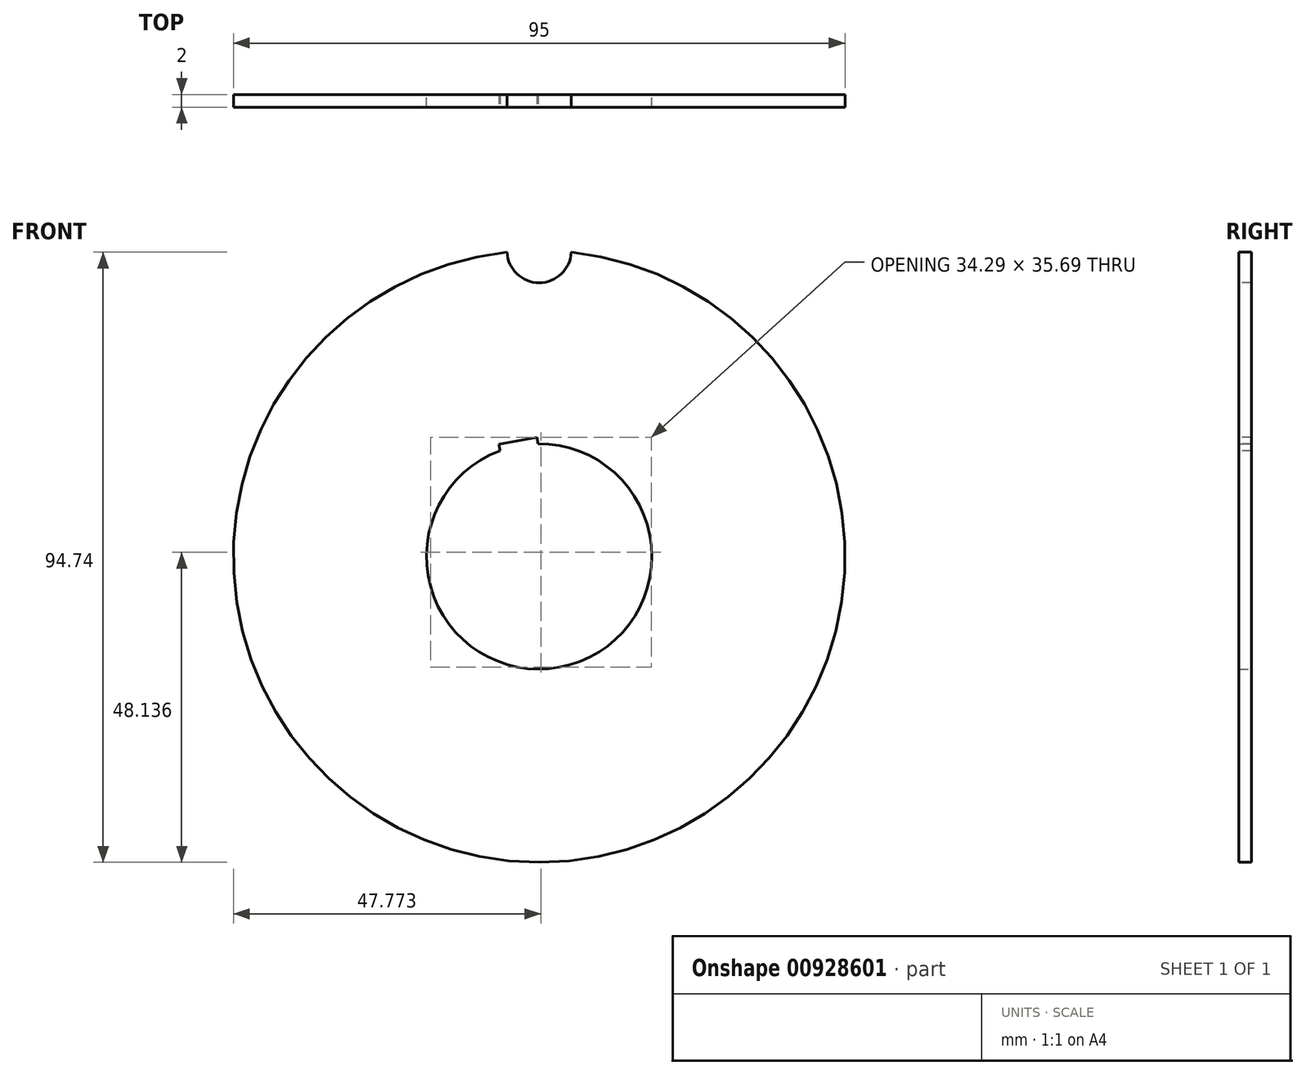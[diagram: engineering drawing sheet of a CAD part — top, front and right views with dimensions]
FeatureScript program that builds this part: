
annotation { "Feature Type Name" : "Feature", "Feature Type Description" : "" }
export const myFeature = defineFeature(function(context is Context, id is Id, definition is map)
    precondition{}
    {
        {
            var Q0;
            Q0=qCreatedBy(makeId("Front.planeOp"),FACE);
            var sketch = newSketch(context, id + "F0", { "sketchPlane" : qUnion([Q0])});
            skCircle(sketch, "E0", {"center": v(0, 0) * mm, "radius": 17.5 * mm});
            skCircle(sketch, "E1", {"center": v(0, 0) * mm, "radius": 47.5 * mm});
            skSolve(sketch);
        }
        {
            var Q0;
            Q0=makeQuery(id+"F0.imprint","IMPRINT",FACE,{"disambiguationData":[TD([[makeQuery(id+"F0.imprint","IMPRINT",EDGE,{"derivedFrom":sQuery(id+"F0.wireOp",EDGE,"E0")}),-1.0]])]});
            extrude(context, id + "F1", {"entities" : qUnion([Q0]), "depth" : 2 * mm, "offsetDistance" : 25 * mm});
        }
        {
            var Q0;
            Q0=makeQuery(id+"F1.opExtrude","CAP_FACE",FACE,{"disambiguationData":[OSD([sQuery(id+"F0.wireOp",EDGE,"E0"),sQuery(id+"F0.wireOp",EDGE,"E1")])],"isStart":false});
            var sketch = newSketch(context, id + "F2", { "sketchPlane" : qUnion([Q0])});
            skLineSegment(sketch, "E2", {"start": v(0, 0) * mm, "end": v(0, 47.5) * mm, "construction": true});
            skLineSegment(sketch, "E3", {"start": v(-5, 47.5) * mm, "end": v(5, 47.5) * mm, "construction": true});
            skArc(sketch, "E4", {"start": v(-5, 47.24) * mm, "mid": v(0, 42.5) * mm, "end": v(5, 47.24) * mm});
            skArc(sketch, "E5.0", {"start": v(5, 47.24) * mm, "mid": v(0, 47.5) * mm, "end": v(-5, 47.24) * mm});
            skSolve(sketch);
        }
        {
            var Q0;
            Q0=makeQuery(id+"F2.imprint","IMPRINT",FACE,{"disambiguationData":[TD([[makeQuery(id+"F2.imprint","IMPRINT",EDGE,{"derivedFrom":sQuery(id+"F2.wireOp",EDGE,"E4")}),1.0]])]});
            extrude(context, id + "F3", {"entities" : qUnion([Q0]), "operationType" : NewBodyOperationType.REMOVE, "endBound" : BoundingType.THROUGH_ALL, "oppositeDirection" : true, "depth" : 25 * mm, "offsetDistance" : 25 * mm});
        }
        {
            var Q0;
            Q0=qCreatedBy(makeId("Right.planeOp"),FACE);
            var sketch = newSketch(context, id + "F4", { "sketchPlane" : qUnion([Q0])});
            skLineSegment(sketch, "E6", {"start": v(0, 0) * mm, "end": v(-101.85, 0) * mm});
            skSolve(sketch);
        }
        {
            var Q0;
            Q0=makeQuery(id+"F1.opExtrude","CAP_FACE",FACE,{"disambiguationData":[OSD([sQuery(id+"F0.wireOp",EDGE,"E0"),sQuery(id+"F0.wireOp",EDGE,"E1")])],"isStart":false});
            var sketch = newSketch(context, id + "F5", { "sketchPlane" : qUnion([Q0])});
            skLineSegment(sketch, "E7", {"start": v(-6.07, 16.41) * mm, "end": v(-6.25, 17.4) * mm});
            skLineSegment(sketch, "E8", {"start": v(-6.25, 17.4) * mm, "end": v(-0.35, 18.48) * mm});
            skLineSegment(sketch, "E9", {"start": v(-0.35, 18.48) * mm, "end": v(-0.17, 17.5) * mm});
            skSolve(sketch);
        }
        {
            var Q0;
            {var subQ0=sQuery(id+"F5.wireOp",EDGE,"E7");Q0=makeQuery(id+"F5.imprint","IMPRINT",FACE,{"disambiguationData":[TD([[makeQuery(id+"F5.imprint","IMPRINT",EDGE,{"derivedFrom":subQ0}),-1.0]])]});}
            extrude(context, id + "F6", {"entities" : qUnion([Q0]), "operationType" : NewBodyOperationType.REMOVE, "oppositeDirection" : true, "depth" : 25 * mm, "offsetDistance" : 25 * mm});
        }
        {
            var Q0;
            Q0=qCreatedBy(makeId("Right.planeOp"),FACE);
            var sketch = newSketch(context, id + "F7", { "sketchPlane" : qUnion([Q0])});
            skLineSegment(sketch, "E10", {"start": v(0, 0) * mm, "end": v(45.61, 0) * mm});
            skSolve(sketch);
        }
    });
